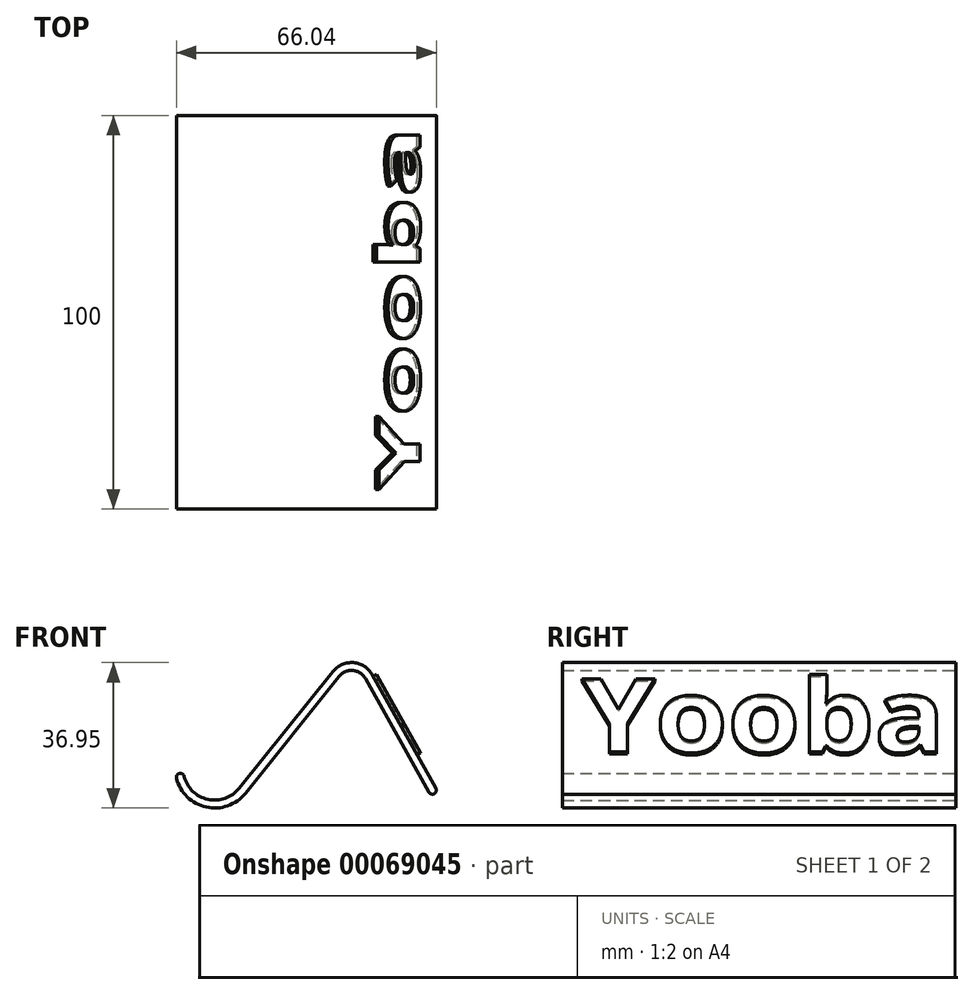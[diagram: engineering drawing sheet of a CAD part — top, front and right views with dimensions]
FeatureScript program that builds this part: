
annotation { "Feature Type Name" : "Feature", "Feature Type Description" : "" }
export const myFeature = defineFeature(function(context is Context, id is Id, definition is map)
    precondition{}
    {
        {
            var Q0;
            Q0=qCreatedBy(makeId("Front.planeOp"),FACE);
            var sketch = newSketch(context, id + "F0", { "sketchPlane" : qUnion([Q0])});
            skLineSegment(sketch, "E0", {"start": v(-29.43, 0) * mm, "end": v(-5.57, 29.71) * mm});
            skLineSegment(sketch, "E1", {"start": v(4.34, 28.89) * mm, "end": v(20.51, 0) * mm});
            skPoint(sketch, "E2.visualSharp", {"position": v(0, 36.65) * mm});
            skArc(sketch, "E2.filletArc", {"start": v(4.34, 28.89) * mm, "mid": v(-0.4, 31.94) * mm, "end": v(-5.57, 29.71) * mm});
            skArc(sketch, "E3", {"start": v(-43.43, 3.07) * mm, "mid": v(-37.38, -2.8) * mm, "end": v(-29.43, 0) * mm});
            skLineSegment(sketch, "E4.0", {"start": v(2.6, 27.9) * mm, "end": v(18.77, -0.98) * mm});
            skArc(sketch, "E4.1", {"start": v(2.6, 27.9) * mm, "mid": v(-0.56, 29.94) * mm, "end": v(-4, 28.46) * mm});
            skLineSegment(sketch, "E4.2", {"start": v(-27.87, -1.25) * mm, "end": v(-4, 28.46) * mm});
            skArc(sketch, "E4.3", {"start": v(-45.37, 2.59) * mm, "mid": v(-37.8, -4.76) * mm, "end": v(-27.87, -1.25) * mm});
            skArc(sketch, "E5", {"start": v(-43.43, 3.07) * mm, "mid": v(-44.64, 3.8) * mm, "end": v(-45.37, 2.59) * mm});
            skArc(sketch, "E6", {"start": v(18.77, -0.98) * mm, "mid": v(20.13, -1.36) * mm, "end": v(20.51, 0) * mm});
            skSolve(sketch);
        }
        {
            var Q0;
            Q0 = qSketchRegion(id + "F0", true);
            extrude(context, id + "F1", {"entities" : qUnion([Q0]), "depth" : 100 * mm});
        }
        {
            var Q0;
            Q0=makeQuery(id+"F1.opExtrude","SWEPT_FACE",FACE,{"disambiguationData":[OSD([sQuery(id+"F0.wireOp",EDGE,"E1")])]});
            var sketch = newSketch(context, id + "F2", { "sketchPlane" : qUnion([Q0])});
            skText(sketch, "E7", { "text": "Yooba", "fontName": "OpenSans-Bold.ttf"});
            const initialGuessF2  = {"E7": [-0.095, -2e-05, 1, 0, 0.02143]};
            skSetInitialGuess(sketch, initialGuessF2);
            skSolve(sketch);
        }
        {
            var Q0;
            Q0 = qSketchRegion(id + "F2", true);
            extrude(context, id + "F3", {"entities" : qUnion([Q0]), "operationType" : NewBodyOperationType.ADD, "depth" : 1 * mm});
        }
    });
